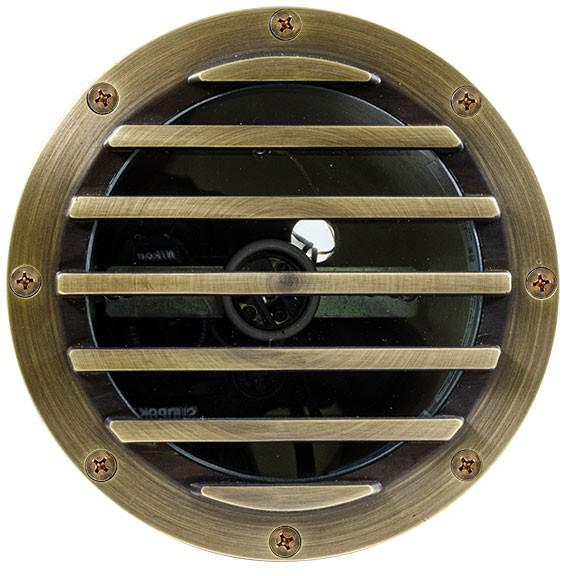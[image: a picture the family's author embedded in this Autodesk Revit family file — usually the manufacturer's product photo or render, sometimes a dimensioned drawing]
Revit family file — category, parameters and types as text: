
# Revit family: Alcon-9094-Revit-Family
name_source: partatom
category: Luminarias
units: mm (PartAtom-declared; Revit-internal decimal feet)

## family parameters
Anfitrión = Cara
Compartido = No
Corte con vacíos al cargar = No
Cota de conector redondo = Usar diámetro
Mantener orientación de anotación = No
Origen de luz = Sí
Punto de cálculo de habitación = No
Tipo de pieza = Normal

## types (1)
- Alcon-9094-Revit-Family
    Cambio de temperatura de color de luz atenuada = <Ninguno>
    Elevación por defecto = 4' - 0"
    Fabricante = Alcon Lighting
    Filtro de color = 16777215
    LENS GLASS = Glass
    Link to IES File = https://www.alconlighting.com
    Longitud de símbolo de origen de luz = 10' - 0"
    Modelo = Alcon Lighting 9094
    Product Data URL = https://www.alconlighting.com
    Product Page = https://www.alconlighting.com
    TOP FINISH = <Por categoría>
    URL = https://www.alconlighting.com
    Ángulo de campo de foco = 90.00°
    Ángulo de enfoque = 30.00°
    Ángulo de inclinación = 60.00°

## geometry (parser evidence)
native form markers: Sweep x3
no freeform markers — native parametric forms only
